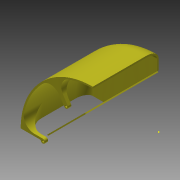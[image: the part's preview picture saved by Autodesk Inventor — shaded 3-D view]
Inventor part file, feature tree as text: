
AUTODESK INVENTOR PART (.ipt)
format: ipt  version: 2015 (Build 190159000, 159)  size: 698,880 bytes
history: native  units: mm
features: sketch x17, extrude x13, revolve x5, fillet x5
ambient origin geometry x8: Origin, YZ Plane, XZ Plane, XY Plane, X Axis, Y Axis, Z Axis, Center Point
bodies: Body1 (feature_tree)
feature tree (40):
  sketch  "Boceto1"  dims[d1=40.0mm d2=20.0mm d3=20.0mm d4=5.0mm d5=360.0deg d6=5.0mm d7=5.0mm d9=5.0mm d10=10.0mm d11=2.451216mm d13=270.0mm]
  revolve  "Revolución1"  [1 undecoded]
  sketch  "Boceto3"  dims[d20=3.0mm d21=120.0mm]
  extrude  "Extrusión2"  Depth=100.0mm
  extrude  "Extrusión3"  Depth=120.0mm
  sketch  "Boceto6"  dims[d22=3.0mm d23=120.0mm]
  revolve  "Revolución2"  [1 undecoded]
  revolve  "Revolución3"  [1 undecoded]
  revolve  "Revolución4"  [1 undecoded]
  revolve  "Revolución5"  [1 undecoded]
  fillet  "Empalme2"  Radius=100.0mm
  sketch  "Boceto7"  dims[d24=90.0deg]
  extrude  "Extrusión7"  Depth=20.0mm
  extrude  "Extrusión8"  Depth=3.0mm
  extrude  "Extrusión9"  TaperAngle=90.0deg  [1 undecoded]
  extrude  "Extrusión10"  TaperAngle=90.0deg  [1 undecoded]
  fillet  "Empalme4"  Radius=3.0mm
  fillet  "Empalme5"  Radius=20.0mm
  sketch  "Boceto16"  dims[d57=135.0mm d58=3.0mm]
  extrude  "Extrusión11"  Depth=10.0mm
  extrude  "Extrusión12"  Depth=10.0mm TaperAngle=0.0deg
  extrude  "Extrusión13"  Depth=8.0mm
  fillet  "Empalme6"  Radius=8.0mm
  extrude  "Extrusión14"  Depth=6.0mm TaperAngle=0.0deg
  extrude  "Extrusión15"  Depth=6.0mm TaperAngle=0.0deg
  extrude  "Extrusión16"  Depth=6.0mm TaperAngle=0.0deg
  extrude  "Extrusión17"  Depth=4.0mm
  fillet  "Empalme7"  Radius=20.0mm
  sketch  "Boceto2"  dims[d14=3.0mm d19=100.0mm]
  sketch  "Boceto11"  dims[d26=40.0mm d27=20.0mm d28=20.0mm d29=5.0mm d30=360.0deg d31=5.0mm d32=5.0mm d33=5.0mm d34=10.0mm d35=2.451216mm d36=270.0mm d37=3.0mm d38=60.0mm d39=0.0mm]
  sketch  "Boceto12"  dims[d40=3.0mm d41=0.0mm d51=20.0mm]
  sketch  "Boceto13"  dims[d52=45.0mm d53=20.0mm d54=100.0mm]
  sketch  "Boceto14"  dims[d55=90.0deg d56=20.0mm]
  sketch  "Boceto17"  dims[d59=90.0deg d60=90.0deg]
  sketch  "Boceto18"  dims[d61=90.0deg d62=90.0deg d63=3.0mm d69=20.0mm]
  sketch  "Boceto19"  dims[d70=10.0mm d71=10.0mm]
  sketch  "Boceto20"  dims[d73=10.0mm d74=111.0mm d75=0.0mm]
  sketch  "Boceto21"  dims[d79=8.0mm d80=8.0mm d81=8.0mm]
  sketch  "Boceto22"  dims[d82=8.0mm d83=6.0mm d84=0.0mm]
  sketch  "Boceto23"  dims[d87=20.0mm d89=360.0deg d91=6.0mm d92=0.0mm d93=6.0mm d94=0.0mm d95=30.0mm d96=20.0mm d97=60.0deg d98=1220.0mm d99=0.0mm d100=888.0mm d101=0.0mm d102=6.0mm d103=0.0mm d104=1.0mm d106=1.0mm d107=0.0mm d108=45.0deg d109=3.0mm d110=10.0mm d111=0.0mm d114=2.0mm d115=0.0mm d116=6.0mm d117=6.0mm d118=2.0mm d119=0.0mm d121=4.0mm]
note: 7 required parameter values undecoded (feature->parameter linkage not recoverable at this tier; creation-order binding heuristic only, values carry confidence <= 0.55)